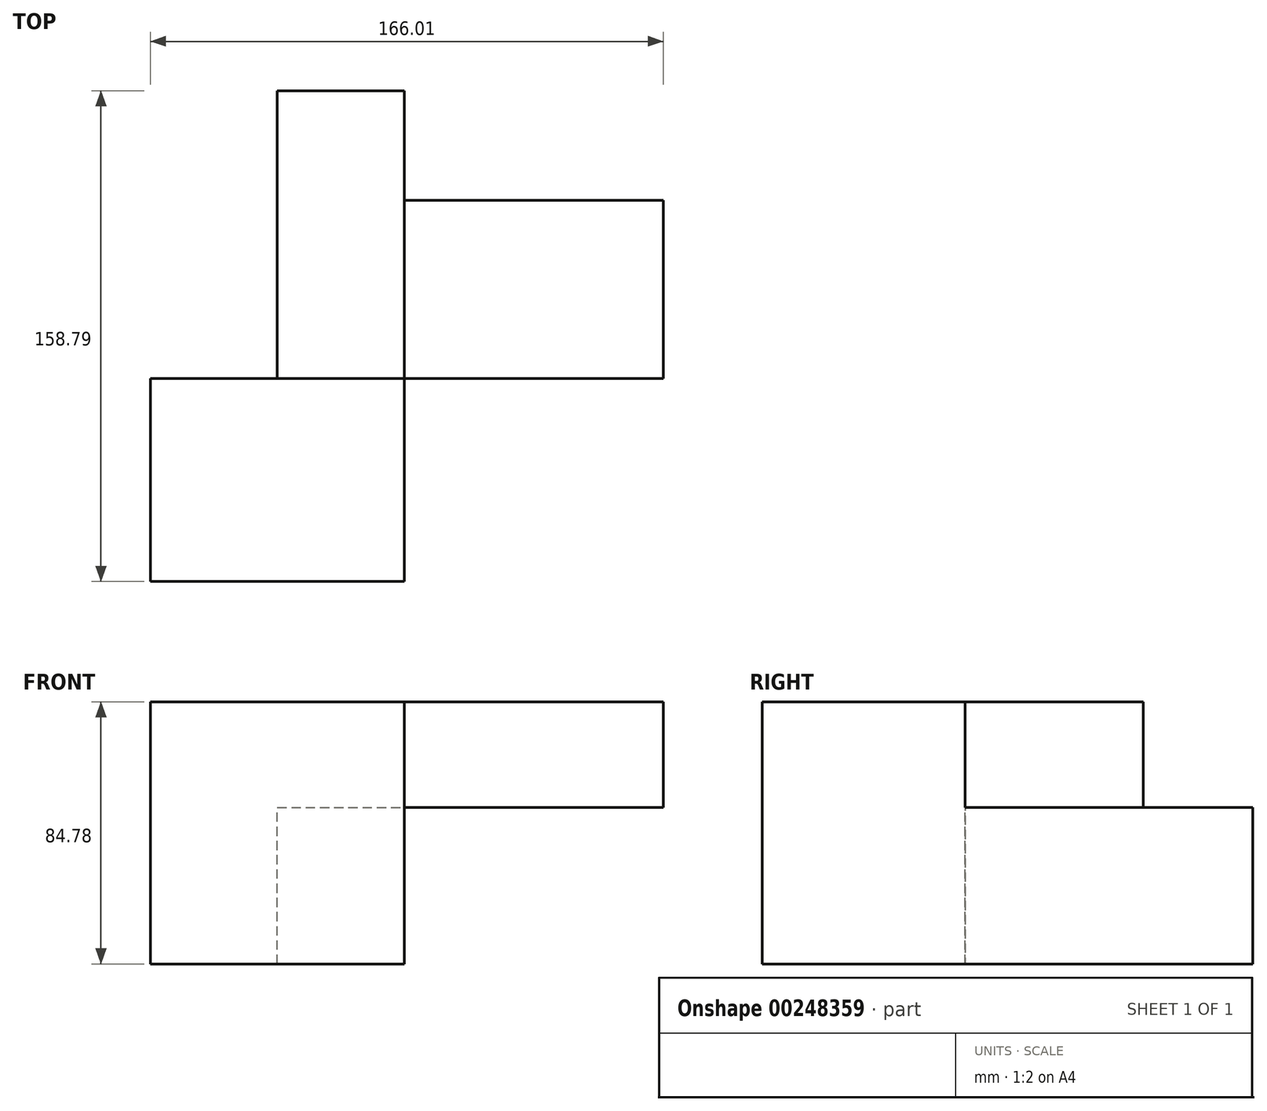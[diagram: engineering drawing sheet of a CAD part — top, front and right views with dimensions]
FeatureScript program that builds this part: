
annotation { "Feature Type Name" : "Feature", "Feature Type Description" : "" }
export const myFeature = defineFeature(function(context is Context, id is Id, definition is map)
    precondition{}
    {
        {
            var Q0;
            Q0=qCreatedBy(makeId("Front.planeOp"),FACE);
            var sketch = newSketch(context, id + "F0", { "sketchPlane" : qUnion([Q0])});
            skLineSegment(sketch, "E0.bottom", {"start": v(0, 34.19) * mm, "end": v(82.2, 34.19) * mm});
            skLineSegment(sketch, "E0.top", {"start": v(0, -50.6) * mm, "end": v(82.2, -50.6) * mm});
            skLineSegment(sketch, "E0.left", {"start": v(0, 34.19) * mm, "end": v(0, -50.6) * mm});
            skLineSegment(sketch, "E0.right", {"start": v(82.2, 34.19) * mm, "end": v(82.2, -50.6) * mm});
            skSolve(sketch);
        }
        {
            var Q0;
            Q0=makeQuery(id+"F0.imprint","IMPRINT",FACE,{"disambiguationData":[TD([[makeQuery(id+"F0.imprint","IMPRINT",EDGE,{"derivedFrom":sQuery(id+"F0.wireOp",EDGE,"E0.bottom")}),-1.0]])]});
            extrude(context, id + "F1", {"entities" : qUnion([Q0]), "depth" : 65.63 * mm});
        }
        {
            var Q0;
            Q0=makeQuery(id+"F1.opExtrude","CAP_FACE",FACE,{"disambiguationData":[OSD([sQuery(id+"F0.wireOp",EDGE,"E0.bottom"),sQuery(id+"F0.wireOp",EDGE,"E0.top"),sQuery(id+"F0.wireOp",EDGE,"E0.left"),sQuery(id+"F0.wireOp",EDGE,"E0.right")])],"isStart":true});
            var sketch = newSketch(context, id + "F2", { "sketchPlane" : qUnion([Q0])});
            skLineSegment(sketch, "E1.bottom", {"start": v(-41.1, -50.6) * mm, "end": v(-82.2, -50.6) * mm});
            skLineSegment(sketch, "E1.top", {"start": v(-41.1, 0) * mm, "end": v(-82.2, 0) * mm});
            skLineSegment(sketch, "E1.left", {"start": v(-41.1, -50.6) * mm, "end": v(-41.1, 0) * mm});
            skLineSegment(sketch, "E1.right", {"start": v(-82.2, -50.6) * mm, "end": v(-82.2, 0) * mm});
            skSolve(sketch);
        }
        {
            var Q0;
            Q0 = qSketchRegion(id + "F2", true);
            extrude(context, id + "F3", {"entities" : qUnion([Q0]), "operationType" : NewBodyOperationType.ADD, "depth" : 93.16 * mm});
        }
        {
            var Q0;
            Q0=makeQuery(id+"F3.boolean.opBoolean","MERGE",FACE,{"derivedFrom":[makeQuery(id+"F1.opExtrude","SWEPT_FACE",FACE,{"disambiguationData":[OSD([sQuery(id+"F0.wireOp",EDGE,"E0.right")])]}),makeQuery(id+"F3.opExtrude","SWEPT_FACE",FACE,{"disambiguationData":[OSD([sQuery(id+"F2.wireOp",EDGE,"E1.right")])]})]});
            var sketch = newSketch(context, id + "F4", { "sketchPlane" : qUnion([Q0])});
            skLineSegment(sketch, "E2.bottom", {"start": v(-39.74, -33.5) * mm, "end": v(57.66, -33.5) * mm});
            skLineSegment(sketch, "E2.top", {"start": v(-39.74, 34.19) * mm, "end": v(57.66, 34.19) * mm});
            skLineSegment(sketch, "E2.left", {"start": v(-39.74, -33.5) * mm, "end": v(-39.74, 34.19) * mm});
            skLineSegment(sketch, "E2.right", {"start": v(57.66, -33.5) * mm, "end": v(57.66, 34.19) * mm});
            skSolve(sketch);
        }
        {
            var Q0;
            {var subQ1=sQuery(id+"F0.wireOp",EDGE,"E0.right");var subQ2=makeQuery(id+"F1.opExtrude","CAP_EDGE",EDGE,{"disambiguationData":[OSD([subQ1])],"isStart":true});Q0=makeQuery(id+"F4.imprint","IMPRINT",FACE,{"disambiguationData":[TD([[makeQuery(id+"F4.imprint","IMPRINT",EDGE,{"derivedFrom":subQ2}),1.0]])]});}
            extrude(context, id + "F5", {"entities" : qUnion([Q0]), "depth" : 83.82 * mm});
        }
    });
